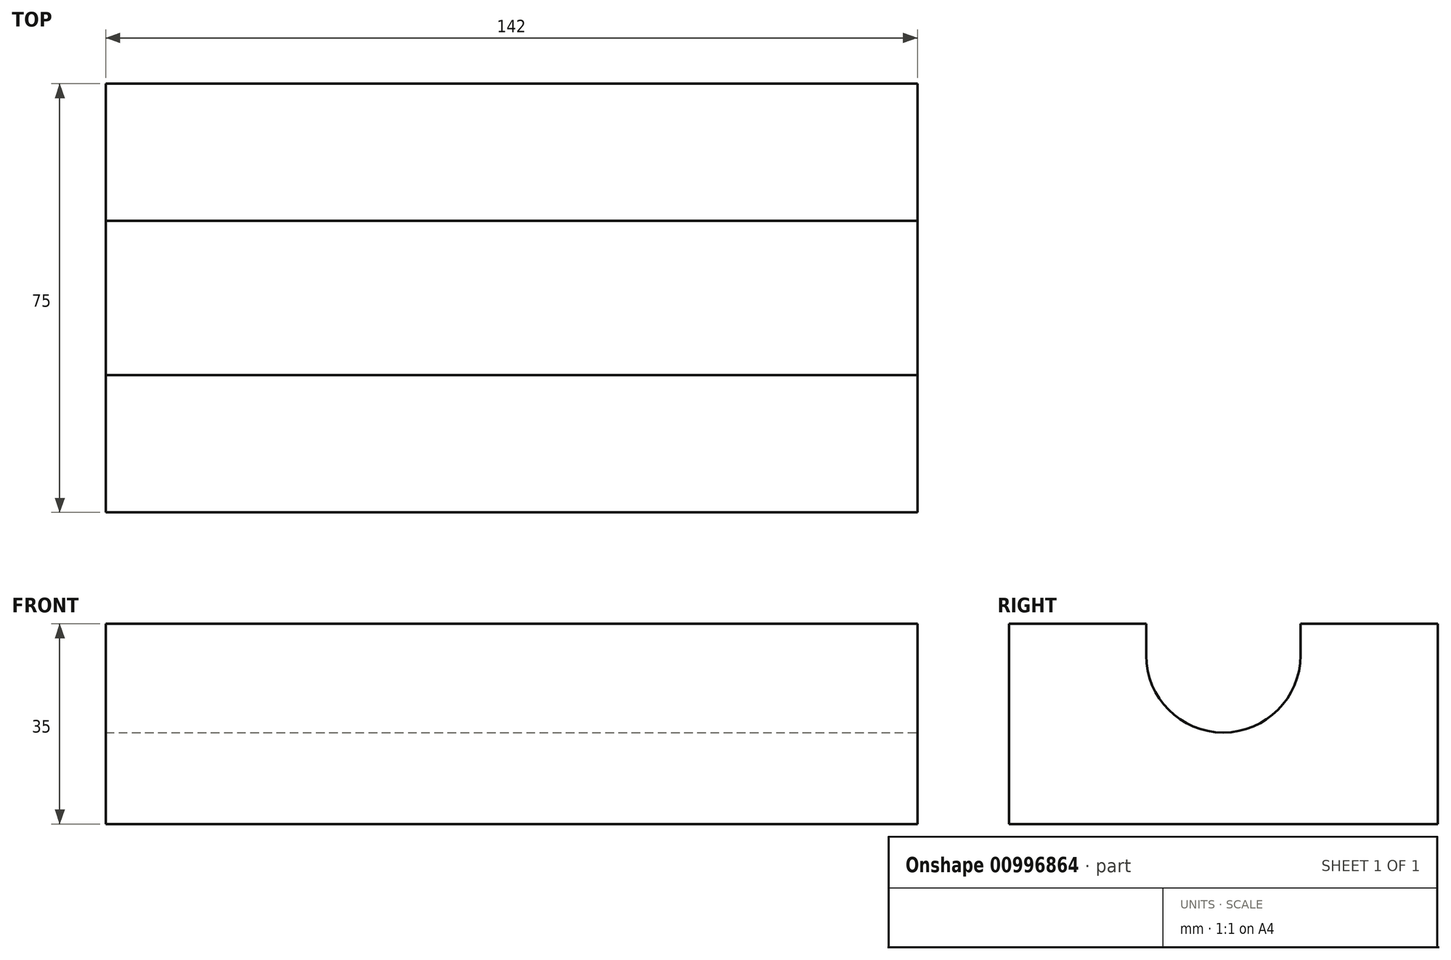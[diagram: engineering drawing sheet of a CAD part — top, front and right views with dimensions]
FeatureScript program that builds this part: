
annotation { "Feature Type Name" : "Feature", "Feature Type Description" : "" }
export const myFeature = defineFeature(function(context is Context, id is Id, definition is map)
    precondition{}
    {
        {
            var Q0;
            Q0=qCreatedBy(makeId("Top.planeOp"),FACE);
            var sketch = newSketch(context, id + "F0", { "sketchPlane" : qUnion([Q0])});
            skLineSegment(sketch, "E0.bottom", {"start": v(71, 37.5) * mm, "end": v(-71, 37.5) * mm});
            skLineSegment(sketch, "E0.top", {"start": v(71, -37.5) * mm, "end": v(-71, -37.5) * mm});
            skLineSegment(sketch, "E0.left", {"start": v(71, 37.5) * mm, "end": v(71, 13.5) * mm});
            skLineSegment(sketch, "E0.right", {"start": v(-71, 37.5) * mm, "end": v(-71, 13.5) * mm});
            skPoint(sketch, "E0.middle", {"position": v(0, 0) * mm});
            skLineSegment(sketch, "E1", {"start": v(-71, 13.5) * mm, "end": v(71, 13.5) * mm});
            skLineSegment(sketch, "E2", {"start": v(-71, -13.5) * mm, "end": v(71, -13.5) * mm});
            skLineSegment(sketch, "E3", {"start": v(71, 13.5) * mm, "end": v(71, -13.5) * mm});
            skLineSegment(sketch, "E4", {"start": v(71, -13.5) * mm, "end": v(71, -37.5) * mm});
            skLineSegment(sketch, "E5", {"start": v(-71, -13.5) * mm, "end": v(-71, -37.5) * mm});
            skLineSegment(sketch, "E6", {"start": v(-71, 13.5) * mm, "end": v(-71, -13.5) * mm});
            skSolve(sketch);
        }
        {
            var Q0;
            Q0=makeQuery(id+"F0.imprint","IMPRINT",FACE,{"disambiguationData":[TD([[makeQuery(id+"F0.imprint","IMPRINT",EDGE,{"derivedFrom":sQuery(id+"F0.wireOp",EDGE,"E0.bottom")}),1.0]])]});
            var Q1;
            Q1=makeQuery(id+"F0.imprint","IMPRINT",FACE,{"disambiguationData":[TD([[makeQuery(id+"F0.imprint","IMPRINT",EDGE,{"derivedFrom":sQuery(id+"F0.wireOp",EDGE,"E1")}),-1.0]])]});
            var Q2;
            Q2=makeQuery(id+"F0.imprint","IMPRINT",FACE,{"disambiguationData":[TD([[makeQuery(id+"F0.imprint","IMPRINT",EDGE,{"derivedFrom":sQuery(id+"F0.wireOp",EDGE,"E0.top")}),-1.0]])]});
            extrude(context, id + "F1", {"entities" : qUnion([Q0, Q1, Q2]), "oppositeDirection" : true, "depth" : 35 * mm, "offsetDistance" : 25 * mm});
        }
        {
            var Q0;
            Q0=makeQuery(id+"F1.opExtrude","SWEPT_FACE",FACE,{"disambiguationData":[OSD([sQuery(id+"F0.wireOp",EDGE,"E0.left"),sQuery(id+"F0.wireOp",EDGE,"E3"),sQuery(id+"F0.wireOp",EDGE,"E4")])]});
            var sketch = newSketch(context, id + "F2", { "sketchPlane" : qUnion([Q0])});
            skPoint(sketch, "E7.0", {"position": v(-13.5, 0) * mm});
            skPoint(sketch, "E8.0", {"position": v(13.5, 0) * mm});
            skLineSegment(sketch, "E9", {"start": v(0, -5.5) * mm, "end": v(0, -19) * mm, "construction": true});
            skArc(sketch, "E10", {"start": v(-13.5, -5.5) * mm, "mid": v(0, -19) * mm, "end": v(13.5, -5.5) * mm});
            skLineSegment(sketch, "E11", {"start": v(-13.5, 0) * mm, "end": v(-13.5, -5.5) * mm});
            skLineSegment(sketch, "E12", {"start": v(13.5, 0) * mm, "end": v(13.5, -5.5) * mm});
            skLineSegment(sketch, "E13", {"start": v(-13.5, -5.5) * mm, "end": v(13.5, -5.5) * mm, "construction": true});
            skSolve(sketch);
        }
        {
            var Q0;
            Q0=makeQuery(id+"F2.imprint","IMPRINT",FACE,{"disambiguationData":[TD([[makeQuery(id+"F2.imprint","IMPRINT",EDGE,{"derivedFrom":sQuery(id+"F2.wireOp",EDGE,"E10")}),1.0]])]});
            extrude(context, id + "F3", {"entities" : qUnion([Q0]), "operationType" : NewBodyOperationType.REMOVE, "endBound" : BoundingType.THROUGH_ALL, "oppositeDirection" : true, "depth" : 25 * mm, "offsetDistance" : 25 * mm});
        }
    });
